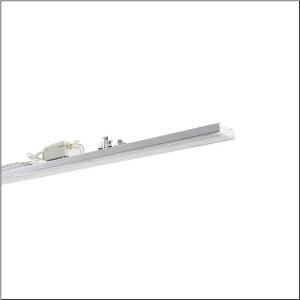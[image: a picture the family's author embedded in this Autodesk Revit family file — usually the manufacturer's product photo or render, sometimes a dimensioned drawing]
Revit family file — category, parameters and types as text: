
# Revit family: licross_r__21_recessed_mo_52tl107n485g_fff6
name_source: partatom
category: Lighting Fixtures
units: mm (PartAtom-declared; Revit-internal decimal feet)

## family parameters
Cut with Voids When Loaded = No
Host = Face
Light Source = No
Part Type = Normal
Room Calculation Point = No
Round Connector Dimension = Use Diameter
Shared = No

## types (1)
- Licross® 21 Recessed MO (1 x LED, 8580 lm, 47.9 W, 4000K)
    Apparent Load = 48 VA
    CIE Flux Codes = 50 81 96 100 100
    Color Rendering = 80
    Color Temperature = 4000K
    Default Elevation = 1800 mm
    Description = Licross® 21 Recessed MO, luminaire insert, of sheet steel, galvanised, coil coated, white, length: 1.500mm, width: 66mm, height: 67mm, LED rated luminous flux: 8.560lm, light colour: 840, control gear: ON/OFF, with plug, 3-pole, with phase selection, mains connection: 220..240V, AC, 50/60Hz, rated input power: 48W, halogen-free wiring, primary optical cover: cover, of PMMA, light emission: direct distribution, primary light characteristic: symmetric, protection rating (complete): IP40, insulation class (complete): insulation class I (protective earthing), certification: CE, ENEC, VDE, UKCA, protection symbol: D if used in an environment without relevant dust loads with corresponding accessories, impact resistance: IK06, permissible ambient temperature for indoor applications: -35..+40°C, corresponds to IFS (International Featured Standards) requirements for safety and quality in the food industry, reducing of maximum allowable ambient temperature of 5°C with ceiling mounting, LABS conformity tested according to VDMA 24364:2018-05, packaging unit: 1 piece
    Height = 58 mm
    Lamp = 1 x LED
    Lamp Light Flux = 8580 lm
    Lamp Power = 47.9 W
    Lamp count = 1
    Length = 1500 mm
    Luminous efficacy = 179 lm/W
    Manufacturer = Siteco
    ModVariant = No
    Model = 52TL107N485G
    Mounting Place = Ceiling
    Mounting Type = Pendant
    Number of Poles = 1
    OnlyDefault = Yes
    Power Factor = 1
    Product Name = Licross® 21 Recessed MO
    Product group = luminaire insert
    ProductGroupID = 901
    Protection Class = Protection class I
    Protection Degree = IP 40
    RLX_Detail_Level = 1
    RLX_Emergency_Light_Flux = 0 lm
    RLX_Emergency_Type = 0
    RLX_Emergency_Type_DB = No
    RlxData = <blob elided: 20745 chars, md5=35ad58df>
    Socket = socket
    Standby Power = 0 W
    System Light Flux = 8580 lm
    System Power = 48 W
    Type Comments = Product without accessories
    Type Image = l_1296930.jpg
    URL = http://relux.com
    VarID = ---
    Voltage = 0 V
    Weight = 0.00 kg
    Width = 66 mm

## geometry (parser evidence)
native form markers: Blend x4, Sweep x12
no freeform markers — native parametric forms only
